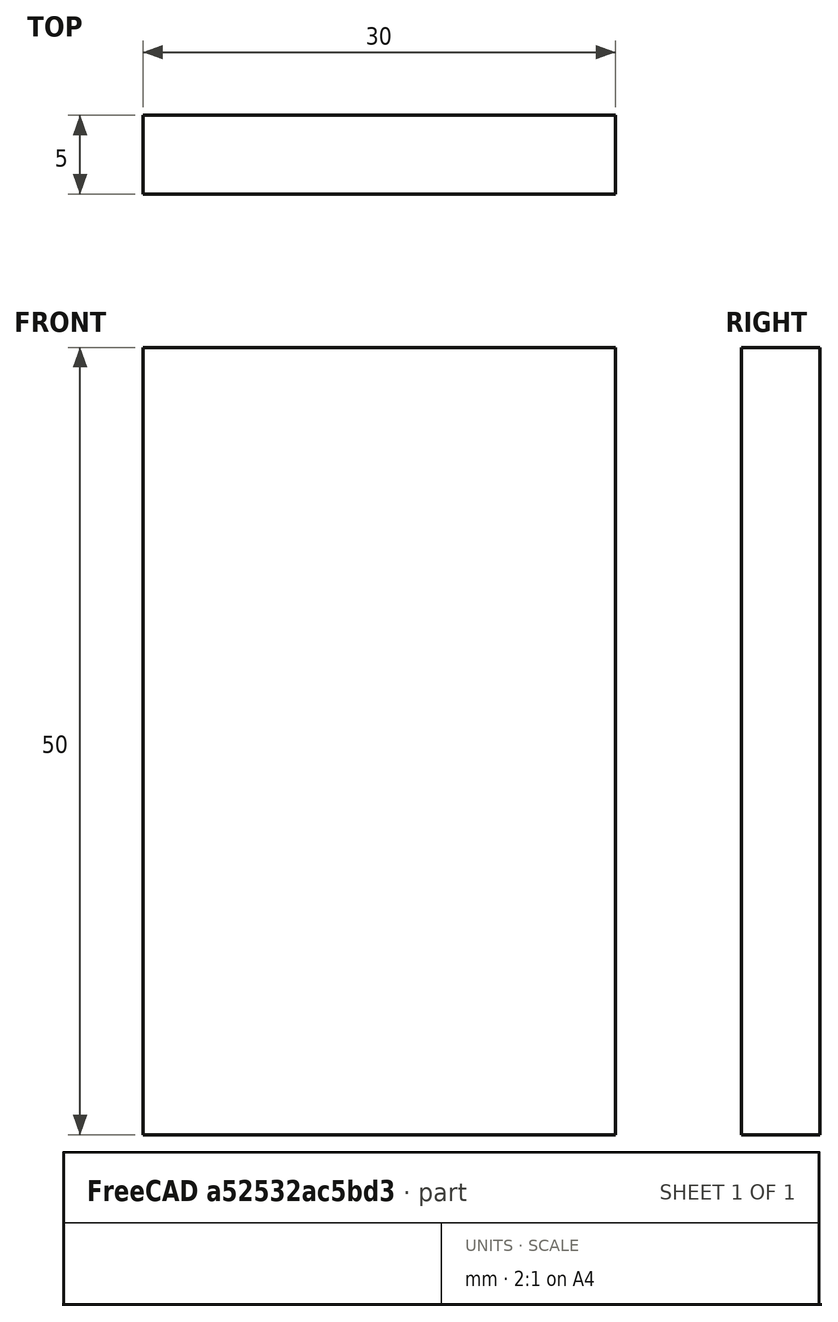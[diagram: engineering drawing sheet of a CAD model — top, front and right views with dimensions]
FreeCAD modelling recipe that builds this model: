
FCSTD DOCUMENT  (FreeCAD 0.15R4671 (Git))
Label: Flat Bar 30x5 EN10058 S235JR
License: All rights reserved
LicenseURL: http://en.wikipedia.org/wiki/All_rights_reserved
objects: Sketcher::SketchObject×1, Part::Extrusion×1
note: 2 computed .brp shape members not serialized (recipe doc carries the construction recipe); baked Part::Feature solids carry a one-line shape summary decoded from their .brp

FEATURE [Sketcher::SketchObject] Sketch
  sketch-geometry (4):
    g0: LineSegment StartX=-15 StartY=-2.5 StartZ=0 EndX=15 EndY=-2.5 EndZ=0
    g1: LineSegment StartX=15 StartY=-2.5 StartZ=0 EndX=15 EndY=2.5 EndZ=0
    g2: LineSegment StartX=15 StartY=2.5 StartZ=0 EndX=-15 EndY=2.5 EndZ=0
    g3: LineSegment StartX=-15 StartY=2.5 StartZ=0 EndX=-15 EndY=-2.5 EndZ=0
  constraints (12):
    c: Coincident(g0,g1)
    c: Coincident(g1,g2)
    c: Coincident(g2,g3)
    c: Coincident(g3,g0)
    c: Horizontal(g0)
    c: Horizontal(g2)
    c: Vertical(g1)
    c: Vertical(g3)
    c: Symmetric(g1,g2,g-2)
    c: Symmetric(g0,g1,g-1)
    c: DistanceY(g1) = 5
    c: DistanceX(g0) = 30
FEATURE [Part::Extrusion] Extrude  label="Flat Bar 30x5 EN10058 S235JR"
  Base = -> Sketch
  Dir = (0,0,50)
  Solid = true
